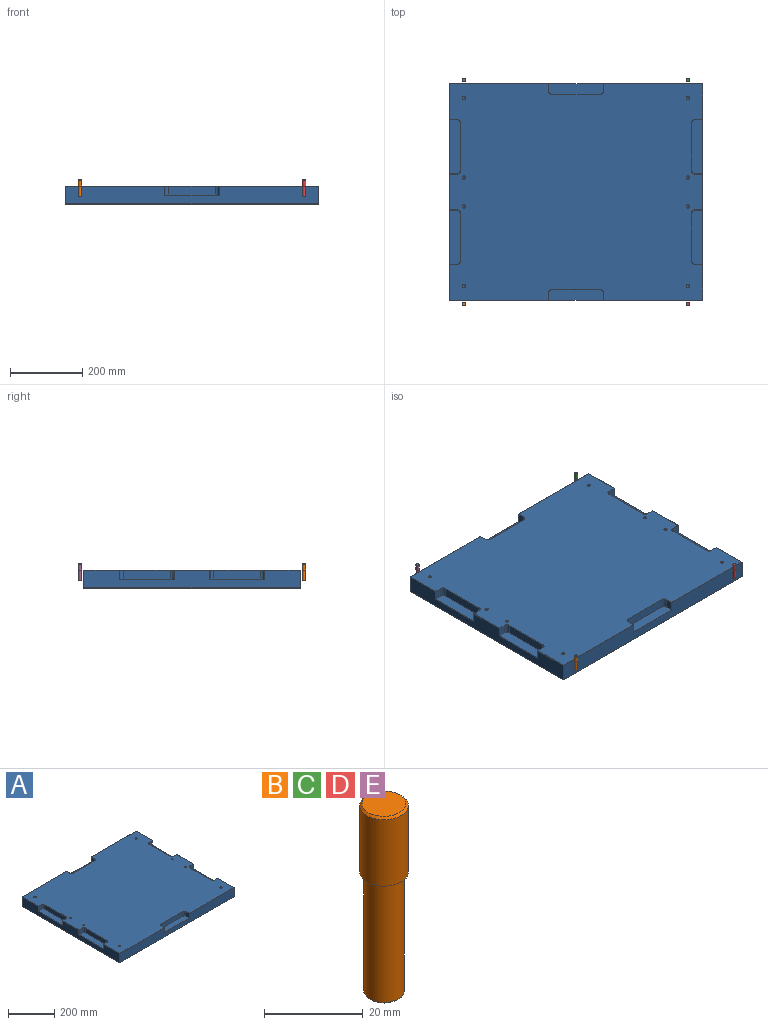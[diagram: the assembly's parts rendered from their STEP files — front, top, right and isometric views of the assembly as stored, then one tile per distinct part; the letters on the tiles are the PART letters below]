
ASSEMBLY  parts=5 mates=4
PART A: 152 faces, bbox 700x600x50 mm
  f0: plane 24.5x19.5mm, normal (0,-1,0), area 477.7mm2, adj f1,f41,f76,f77
  f1: cylinder r=10mm len=24.5mm, axis (0,0,-1), area 384.8mm2, adj f0,f2,f41,f65
  f2: plane 130x24.5mm, normal (-1,0,0), area 3185mm2, adj f1,f3,f41,f59
  f3: cylinder r=10mm len=24.5mm, axis (0,0,-1), area 384.8mm2, adj f2,f4,f41,f67
  f4: plane 24.5x19.5mm, normal (0,1,0), area 477.7mm2, adj f3,f41,f78,f79
  f5: plane 24.5x19.5mm, normal (1,0,0), area 477.7mm2, adj f6,f40,f80,f81
  f6: cylinder r=10mm len=24.5mm, axis (0,0,-1), area 384.8mm2, adj f5,f7,f40,f68
  f7: plane 130x24.5mm, normal (0,-1,0), area 3185mm2, adj f6,f8,f40,f60
  f8: cylinder r=10mm len=24.5mm, axis (0,0,-1), area 384.8mm2, adj f7,f9,f40,f61
  f9: plane 24.5x19.5mm, normal (-1,0,0), area 477.7mm2, adj f8,f40,f70,f71
  f10: plane 699x49mm, normal (0,-1,0), area 30476mm2, adj f69,f70,f81,f88,f95,f102,f107,f108
  f11: plane 24.5x19.5mm, normal (0,1,0), area 477.7mm2, adj f12,f39,f72,f73
  f12: cylinder r=10mm len=24.5mm, axis (0,0,-1), area 384.8mm2, adj f11,f13,f39,f62
  f13: plane 130x24.5mm, normal (1,0,0), area 3185mm2, adj f12,f14,f39,f58
  f14: cylinder r=10mm len=24.5mm, axis (0,0,-1), area 384.8mm2, adj f13,f15,f39,f64
  f15: plane 24.5x19.5mm, normal (0,-1,0), area 477.7mm2, adj f14,f39,f74,f75
  f16: plane 24.5x19.5mm, normal (0,1,0), area 477.7mm2, adj f17,f38,f91,f103
  f17: cylinder r=10mm len=24.5mm, axis (0,0,-1), area 384.8mm2, adj f16,f18,f38,f98
  f18: plane 130x24.5mm, normal (1,0,0), area 3185mm2, adj f17,f19,f38,f104
  f19: cylinder r=10mm len=24.5mm, axis (0,0,-1), area 384.8mm2, adj f18,f20,f38,f111
  f20: plane 24.5x19.5mm, normal (0,-1,0), area 477.7mm2, adj f19,f38,f116,f117
  f21: plane 599x49mm, normal (1,0,0), area 21801mm2, adj f63,f73,f74,f89,f90,f102,f103,f110
  f22: plane 24.5x19.5mm, normal (-1,0,0), area 477.7mm2, adj f23,f37,f136,f141
  f23: cylinder r=10mm len=24.5mm, axis (0,0,-1), area 384.8mm2, adj f22,f24,f37,f132
  f24: plane 130x24.5mm, normal (0,1,0), area 3185mm2, adj f23,f25,f37,f128
  f25: cylinder r=10mm len=24.5mm, axis (0,0,-1), area 384.8mm2, adj f24,f26,f37,f133
  f26: plane 24.5x19.5mm, normal (1,0,0), area 477.7mm2, adj f25,f37,f137,f142
  f27: plane 699x49mm, normal (0,1,0), area 30476mm2, adj f121,f126,f130,f135,f138,f141,f142,f143
  f28: plane 599x49mm, normal (-1,0,0), area 21801mm2, adj f66,f77,f78,f93,f94,f106,f107,f113
  f29: plane 24.5x19.5mm, normal (0,-1,0), area 477.7mm2, adj f30,f36,f118,f119
  f30: cylinder r=10mm len=24.5mm, axis (0,0,-1), area 384.8mm2, adj f29,f31,f36,f112
  f31: plane 130x24.5mm, normal (-1,0,0), area 3185mm2, adj f30,f32,f36,f105
  f32: cylinder r=10mm len=24.5mm, axis (0,0,-1), area 384.8mm2, adj f31,f33,f36,f99
  f33: plane 24.5x19.5mm, normal (0,1,0), area 477.7mm2, adj f32,f36,f92,f106
  f34: plane 699x599mm, normal (0,0,1), area 391296mm2, adj f58,f59,f60,f61,f62,f64,f65,f67
  f35: plane 699x599mm, normal (0,0,-1), area 418701mm2, adj f108,f115,f120,f121
  f36: plane 150x29.5mm, normal (0,0,1), area 4382.1mm2, adj f29,f30,f31,f32,f33,f113
  f37: plane 150x29.5mm, normal (0,0,1), area 4382.1mm2, adj f22,f23,f24,f25,f26,f143
  f38: plane 150x29.5mm, normal (0,0,1), area 4382.1mm2, adj f16,f17,f18,f19,f20,f110
  f39: plane 150x29.5mm, normal (0,0,1), area 4382.1mm2, adj f11,f12,f13,f14,f15,f63
  f40: plane 150x29.5mm, normal (0,0,1), area 4382.1mm2, adj f5,f6,f7,f8,f9,f69
  f41: plane 150x29.5mm, normal (0,0,1), area 4382.1mm2, adj f0,f1,f2,f3,f4,f66
  f42: cone r=0mm half-angle=59deg, axis (0,0,1), area 58.6mm2, adj f43
  f43: cylinder r=4mm len=34.5mm, axis (0,0,1), area 867.1mm2, adj f42,f151
  f44: cone r=0mm half-angle=59deg, axis (0,0,1), area 58.6mm2, adj f45
  f45: cylinder r=4mm len=34.5mm, axis (0,0,1), area 867.1mm2, adj f44,f150
  f46: cone r=0mm half-angle=59deg, axis (0,0,1), area 58.6mm2, adj f47
  f47: cylinder r=4mm len=34.5mm, axis (0,0,1), area 867.1mm2, adj f46,f149
  f48: cone r=0mm half-angle=59deg, axis (0,0,1), area 58.6mm2, adj f49
  f49: cylinder r=4mm len=34.5mm, axis (0,0,1), area 867.1mm2, adj f48,f148
  f50: cone r=0mm half-angle=59deg, axis (0,0,1), area 58.6mm2, adj f51
  f51: cylinder r=4mm len=34.5mm, axis (0,0,1), area 867.1mm2, adj f50,f147
  f52: cone r=0mm half-angle=59deg, axis (0,0,1), area 58.6mm2, adj f53
  f53: cylinder r=4mm len=34.5mm, axis (0,0,1), area 867.1mm2, adj f52,f146
  f54: cone r=0mm half-angle=59deg, axis (0,0,1), area 58.6mm2, adj f55
  f55: cylinder r=4mm len=34.5mm, axis (0,0,1), area 867.1mm2, adj f54,f145
  f56: cone r=0mm half-angle=59deg, axis (0,0,1), area 58.6mm2, adj f57
  f57: cylinder r=4mm len=34.5mm, axis (0,0,1), area 867.1mm2, adj f56,f144
  f58: plane 130x0.5mm, normal (0.71,0,0.71), area 91.9mm2, adj f13,f34,f62,f64
  f59: plane 130x0.5mm, normal (-0.71,0,0.71), area 91.9mm2, adj f2,f34,f65,f67
  f60: plane 130x0.5mm, normal (0,-0.71,0.71), area 91.9mm2, adj f7,f34,f61,f68
  f61: cone r=10mm half-angle=45deg, axis (0,0,1), area 11.4mm2, adj f8,f34,f60,f71
  f62: cone r=10mm half-angle=45deg, axis (0,0,1), area 11.4mm2, adj f12,f34,f58,f72
  f63: plane 151x0.5mm, normal (0.71,0,0.71), area 106.4mm2, adj f21,f39,f73,f74
  f64: cone r=10mm half-angle=45deg, axis (0,0,1), area 11.4mm2, adj f14,f34,f58,f75
  f65: cone r=10.5mm half-angle=45deg, axis (0,0,1), area 11.4mm2, adj f1,f34,f59,f76
  f66: plane 151x0.5mm, normal (-0.71,0,0.71), area 106.4mm2, adj f28,f41,f77,f78
  f67: cone r=10.5mm half-angle=45deg, axis (0,0,1), area 11.4mm2, adj f3,f34,f59,f79
  f68: cone r=10mm half-angle=45deg, axis (0,0,1), area 11.4mm2, adj f6,f34,f60,f80
  f69: plane 151x0.5mm, normal (0,-0.71,0.71), area 106.4mm2, adj f10,f40,f70,f81
  f70: plane 25x0.5mm, normal (-0.71,-0.71,0), area 17.5mm2, adj f9,f10,f69,f82
  f71: plane 19.5x0.5mm, normal (-0.71,0,0.71), area 13.8mm2, adj f9,f34,f61,f82
  f72: plane 19.5x0.5mm, normal (0,0.71,0.71), area 13.8mm2, adj f11,f34,f62,f83
  f73: plane 25x0.5mm, normal (0.71,0.71,0), area 17.5mm2, adj f11,f21,f63,f83
  f74: plane 25x0.5mm, normal (0.71,-0.71,0), area 17.5mm2, adj f15,f21,f63,f84
  f75: plane 19.5x0.5mm, normal (0,-0.71,0.71), area 13.8mm2, adj f15,f34,f64,f84
  f76: plane 19.5x0.5mm, normal (0,-0.71,0.71), area 13.8mm2, adj f0,f34,f65,f85
  f77: plane 25x0.5mm, normal (-0.71,-0.71,0), area 17.5mm2, adj f0,f28,f66,f85
  f78: plane 25x0.5mm, normal (-0.71,0.71,0), area 17.5mm2, adj f4,f28,f66,f86
  f79: plane 19.5x0.5mm, normal (0,0.71,0.71), area 13.8mm2, adj f4,f34,f67,f86
  f80: plane 19.5x0.5mm, normal (0.71,0,0.71), area 13.8mm2, adj f5,f34,f68,f87
  f81: plane 25x0.5mm, normal (0.71,-0.71,0), area 17.5mm2, adj f5,f10,f69,f87
  f82: plane 0.5x0.5mm, normal (-0.58,-0.58,0.58), area 0.2mm2, adj f70,f71,f88
  f83: plane 0.5x0.5mm, normal (0.58,0.58,0.58), area 0.2mm2, adj f72,f73,f89
  f84: plane 0.5x0.5mm, normal (0.58,-0.58,0.58), area 0.2mm2, adj f74,f75,f90
  f85: plane 0.5x0.5mm, normal (-0.58,-0.58,0.58), area 0.2mm2, adj f76,f77,f93
  f86: plane 0.5x0.5mm, normal (-0.58,0.58,0.58), area 0.2mm2, adj f78,f79,f94
  f87: plane 0.5x0.5mm, normal (0.58,-0.58,0.58), area 0.2mm2, adj f80,f81,f95
  f88: plane 274x0.5mm, normal (0,-0.71,0.71), area 193.7mm2, adj f10,f34,f82,f96
  f89: plane 99x0.5mm, normal (0.71,0,0.71), area 70mm2, adj f21,f34,f83,f96
  f90: plane 99x0.5mm, normal (0.71,0,0.71), area 70mm2, adj f21,f34,f84,f97
  f91: plane 19.5x0.5mm, normal (0,0.71,0.71), area 13.8mm2, adj f16,f34,f97,f98
  f92: plane 19.5x0.5mm, normal (0,0.71,0.71), area 13.8mm2, adj f33,f34,f99,f100
  f93: plane 99x0.5mm, normal (-0.71,0,0.71), area 70mm2, adj f28,f34,f85,f100
  f94: plane 99x0.5mm, normal (-0.71,0,0.71), area 70mm2, adj f28,f34,f86,f101
  f95: plane 274x0.5mm, normal (0,-0.71,0.71), area 193.7mm2, adj f10,f34,f87,f101
  f96: plane 0.5x0.5mm, normal (0.58,-0.58,0.58), area 0.2mm2, adj f88,f89,f102
  f97: plane 0.5x0.5mm, normal (0.58,0.58,0.58), area 0.2mm2, adj f90,f91,f103
  f98: cone r=10mm half-angle=45deg, axis (0,0,1), area 11.4mm2, adj f17,f34,f91,f104
  f99: cone r=10mm half-angle=45deg, axis (0,0,1), area 11.4mm2, adj f32,f34,f92,f105
  f100: plane 0.5x0.5mm, normal (-0.58,0.58,0.58), area 0.2mm2, adj f92,f93,f106
  f101: plane 0.5x0.5mm, normal (-0.58,-0.58,0.58), area 0.2mm2, adj f94,f95,f107
  f102: plane 49x0.5mm, normal (0.71,-0.71,0), area 34.6mm2, adj f10,f21,f96,f109
  f103: plane 25x0.5mm, normal (0.71,0.71,0), area 17.5mm2, adj f16,f21,f97,f110
  f104: plane 130x0.5mm, normal (0.71,0,0.71), area 91.9mm2, adj f18,f34,f98,f111
  f105: plane 130x0.5mm, normal (-0.71,0,0.71), area 91.9mm2, adj f31,f34,f99,f112
  f106: plane 25x0.5mm, normal (-0.71,0.71,0), area 17.5mm2, adj f28,f33,f100,f113
  f107: plane 49x0.5mm, normal (-0.71,-0.71,0), area 34.6mm2, adj f10,f28,f101,f114
  f108: plane 699x0.5mm, normal (0,-0.71,-0.71), area 494.3mm2, adj f10,f35,f109,f114
  f109: plane 0.5x0.5mm, normal (0.58,-0.58,-0.58), area 0.2mm2, adj f102,f108,f115
  f110: plane 151x0.5mm, normal (0.71,0,0.71), area 106.4mm2, adj f21,f38,f103,f116
  f111: cone r=10mm half-angle=45deg, axis (0,0,1), area 11.4mm2, adj f19,f34,f104,f117
  f112: cone r=10mm half-angle=45deg, axis (0,0,1), area 11.4mm2, adj f30,f34,f105,f118
  f113: plane 151x0.5mm, normal (-0.71,0,0.71), area 106.4mm2, adj f28,f36,f106,f119
  f114: plane 0.5x0.5mm, normal (-0.58,-0.58,-0.58), area 0.2mm2, adj f107,f108,f120
  f115: plane 599x0.5mm, normal (0.71,0,-0.71), area 423.6mm2, adj f21,f35,f109,f122
  f116: plane 25x0.5mm, normal (0.71,-0.71,0), area 17.5mm2, adj f20,f21,f110,f123
  f117: plane 19.5x0.5mm, normal (0,-0.71,0.71), area 13.8mm2, adj f20,f34,f111,f123
  f118: plane 19.5x0.5mm, normal (0,-0.71,0.71), area 13.8mm2, adj f29,f34,f112,f124
  f119: plane 25x0.5mm, normal (-0.71,-0.71,0), area 17.5mm2, adj f28,f29,f113,f124
  f120: plane 599x0.5mm, normal (-0.71,0,-0.71), area 423.6mm2, adj f28,f35,f114,f125
  f121: plane 699x0.5mm, normal (0,0.71,-0.71), area 494.3mm2, adj f27,f35,f122,f125
  f122: plane 0.5x0.5mm, normal (0.58,0.58,-0.58), area 0.2mm2, adj f115,f121,f126
  f123: plane 0.5x0.5mm, normal (0.58,-0.58,0.58), area 0.2mm2, adj f116,f117,f127
  f124: plane 0.5x0.5mm, normal (-0.58,-0.58,0.58), area 0.2mm2, adj f118,f119,f129
  f125: plane 0.5x0.5mm, normal (-0.58,0.58,-0.58), area 0.2mm2, adj f120,f121,f130
  f126: plane 49x0.5mm, normal (0.71,0.71,0), area 34.6mm2, adj f21,f27,f122,f131
  f127: plane 99x0.5mm, normal (0.71,0,0.71), area 70mm2, adj f21,f34,f123,f131
  f128: plane 130x0.5mm, normal (0,0.71,0.71), area 91.9mm2, adj f24,f34,f132,f133
  f129: plane 99x0.5mm, normal (-0.71,0,0.71), area 70mm2, adj f28,f34,f124,f134
  f130: plane 49x0.5mm, normal (-0.71,0.71,0), area 34.6mm2, adj f27,f28,f125,f134
  f131: plane 0.5x0.5mm, normal (0.58,0.58,0.58), area 0.2mm2, adj f126,f127,f135
  f132: cone r=10mm half-angle=45deg, axis (0,0,1), area 11.4mm2, adj f23,f34,f128,f136
  f133: cone r=10mm half-angle=45deg, axis (0,0,1), area 11.4mm2, adj f25,f34,f128,f137
  f134: plane 0.5x0.5mm, normal (-0.58,0.58,0.58), area 0.2mm2, adj f129,f130,f138
  f135: plane 274x0.5mm, normal (0,0.71,0.71), area 193.7mm2, adj f27,f34,f131,f139
  f136: plane 19.5x0.5mm, normal (-0.71,0,0.71), area 13.8mm2, adj f22,f34,f132,f139
  f137: plane 19.5x0.5mm, normal (0.71,0,0.71), area 13.8mm2, adj f26,f34,f133,f140
  f138: plane 274x0.5mm, normal (0,0.71,0.71), area 193.7mm2, adj f27,f34,f134,f140
  f139: plane 0.5x0.5mm, normal (-0.58,0.58,0.58), area 0.2mm2, adj f135,f136,f141
  f140: plane 0.5x0.5mm, normal (0.58,0.58,0.58), area 0.2mm2, adj f137,f138,f142
  f141: plane 25x0.5mm, normal (-0.71,0.71,0), area 17.5mm2, adj f22,f27,f139,f143
  f142: plane 25x0.5mm, normal (0.71,0.71,0), area 17.5mm2, adj f26,f27,f140,f143
  f143: plane 151x0.5mm, normal (0,0.71,0.71), area 106.4mm2, adj f27,f37,f141,f142
  f144: cone r=4mm half-angle=45deg, axis (0,0,1), area 18.9mm2, adj f34,f57
  f145: cone r=4mm half-angle=45deg, axis (0,0,1), area 18.9mm2, adj f34,f55
  f146: cone r=4mm half-angle=45deg, axis (0,0,1), area 18.9mm2, adj f34,f53
  f147: cone r=4mm half-angle=45deg, axis (0,0,1), area 18.9mm2, adj f34,f51
  f148: cone r=4mm half-angle=45deg, axis (0,0,1), area 18.9mm2, adj f34,f49
  f149: cone r=4mm half-angle=45deg, axis (0,0,1), area 18.9mm2, adj f34,f47
  f150: cone r=4mm half-angle=45deg, axis (0,0,1), area 18.9mm2, adj f34,f45
  f151: cone r=4mm half-angle=45deg, axis (0,0,1), area 18.9mm2, adj f34,f43
PART B: 7 faces, bbox 9.9x9.9x47 mm
  f0: cylinder r=4.95mm len=16.5mm, axis (0,0,-1), area 513.2mm2, adj f2,f6
  f1: plane 8.9x8.9mm, normal (0,0,1), area 62.2mm2, adj f6
  f2: plane 9.9x9.9mm, normal (0,0,-1), area 24.2mm2, adj f0,f3
  f3: cylinder r=4.1mm len=29.5mm, axis (0,0,1), area 760mm2, adj f2,f5
  f4: plane 7.2x7.2mm, normal (0,0,-1), area 40.7mm2, adj f5
  f5: cone r=4.1mm half-angle=45deg, axis (0,0,1), area 17.1mm2, adj f3,f4
  f6: cone r=4.45mm half-angle=45deg, axis (0,0,-1), area 20.9mm2, adj f0,f1
PART C: same geometry as B
PART D: same geometry as B
PART E: same geometry as B
PLACE A rot(axis=(0,0,1),0deg) t=(198.87,-26.68,-251.63)mm fixed
PLACE B rot(axis=(0,0,1),0deg) t=(-111.13,-336.68,-201.63)mm
PLACE C rot(axis=(0,0,1),0deg) t=(508.87,283.32,-201.63)mm
PLACE D rot(axis=(0,0,1),0deg) t=(508.87,-336.68,-201.63)mm
PLACE E rot(axis=(0,0,1),0deg) t=(-111.13,283.32,-201.63)mm
MATE slider D.f0 <-> A.f34  axis (0,0,-1) through (508.87,-336.68,-201.63)mm
MATE slider B.f0 <-> A.f34  axis (0,0,-1) through (-111.13,-336.68,-201.63)mm
MATE slider E.f0 <-> A.f34  axis (0,0,-1) through (-111.13,283.32,-201.63)mm
MATE slider C.f0 <-> A.f34  axis (0,0,-1) through (508.87,283.32,-201.63)mm
